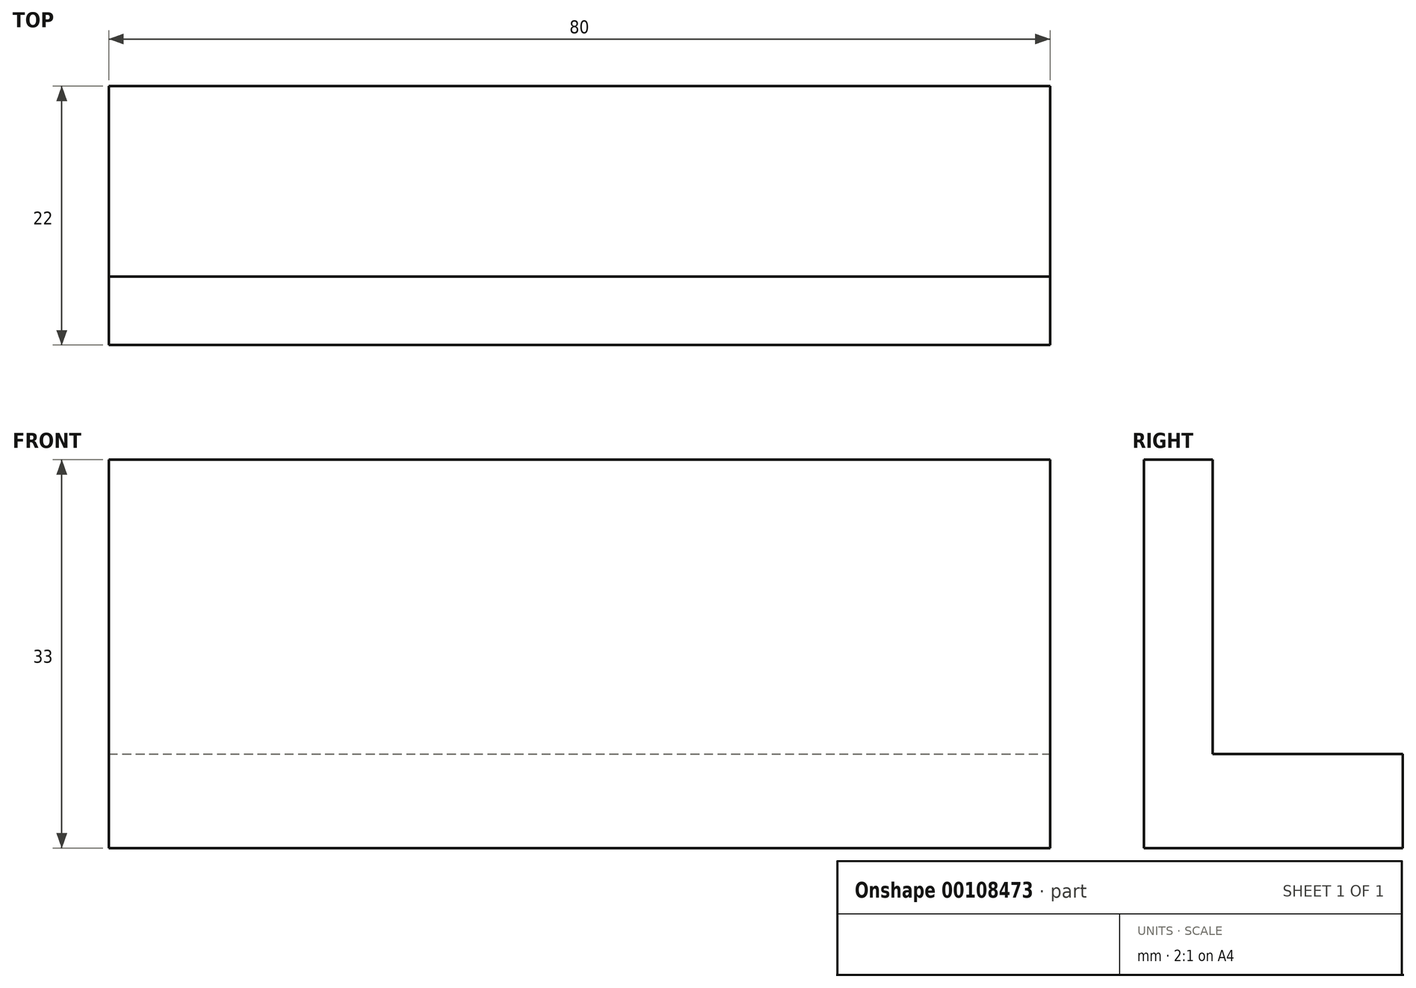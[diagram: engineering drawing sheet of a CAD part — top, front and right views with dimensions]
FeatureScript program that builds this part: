
annotation { "Feature Type Name" : "Feature", "Feature Type Description" : "" }
export const myFeature = defineFeature(function(context is Context, id is Id, definition is map)
    precondition{}
    {
        {
            var Q0;
            Q0=qCreatedBy(makeId("Top.planeOp"),FACE);
            var sketch = newSketch(context, id + "F0", { "sketchPlane" : qUnion([Q0])});
            skLineSegment(sketch, "E0.bottom", {"start": v(-22.9, 5.54) * mm, "end": v(57.1, 5.54) * mm});
            skLineSegment(sketch, "E0.top", {"start": v(-22.9, -9.46) * mm, "end": v(57.1, -9.46) * mm});
            skLineSegment(sketch, "E0.left", {"start": v(-22.9, 5.54) * mm, "end": v(-22.9, -9.46) * mm});
            skLineSegment(sketch, "E0.right", {"start": v(57.1, 5.54) * mm, "end": v(57.1, -9.46) * mm});
            skSolve(sketch);
        }
        {
            var Q0;
            Q0 = qSketchRegion(id + "F0", true);
            extrude(context, id + "F1", {"entities" : qUnion([Q0]), "depth" : 8 * mm});
        }
        {
            var Q0;
            Q0=makeQuery(id+"F1.opExtrude","CAP_FACE",FACE,{"disambiguationData":[OSD([sQuery(id+"F0.wireOp",EDGE,"E0.bottom"),sQuery(id+"F0.wireOp",EDGE,"E0.top"),sQuery(id+"F0.wireOp",EDGE,"E0.left"),sQuery(id+"F0.wireOp",EDGE,"E0.right")])],"isStart":false});
            var sketch = newSketch(context, id + "F2", { "sketchPlane" : qUnion([Q0])});
            skLineSegment(sketch, "E1.bottom", {"start": v(-22.9, -3.64) * mm, "end": v(57.1, -3.64) * mm});
            skLineSegment(sketch, "E1.top", {"start": v(-22.9, -9.46) * mm, "end": v(57.1, -9.46) * mm});
            skLineSegment(sketch, "E1.left", {"start": v(-22.9, -3.64) * mm, "end": v(-22.9, -9.46) * mm});
            skLineSegment(sketch, "E1.right", {"start": v(57.1, -3.64) * mm, "end": v(57.1, -9.46) * mm});
            skSolve(sketch);
        }
        {
            var Q0;
            Q0=makeQuery(id+"F2.imprint","IMPRINT",FACE,{"disambiguationData":[TD([[makeQuery(id+"F2.imprint","IMPRINT",EDGE,{"derivedFrom":sQuery(id+"F2.wireOp",EDGE,"E1.bottom")}),-1.0]])]});
            extrude(context, id + "F3", {"entities" : qUnion([Q0]), "operationType" : NewBodyOperationType.ADD, "depth" : 25 * mm});
        }
        {
            var Q0;
            Q0=makeQuery(id+"F1.opExtrude","SWEPT_FACE",FACE,{"disambiguationData":[OSD([sQuery(id+"F0.wireOp",EDGE,"E0.bottom")])]});
            extrude(context, id + "F4", {"entities" : qUnion([Q0]), "operationType" : NewBodyOperationType.ADD, "depth" : 7 * mm});
        }
    });
